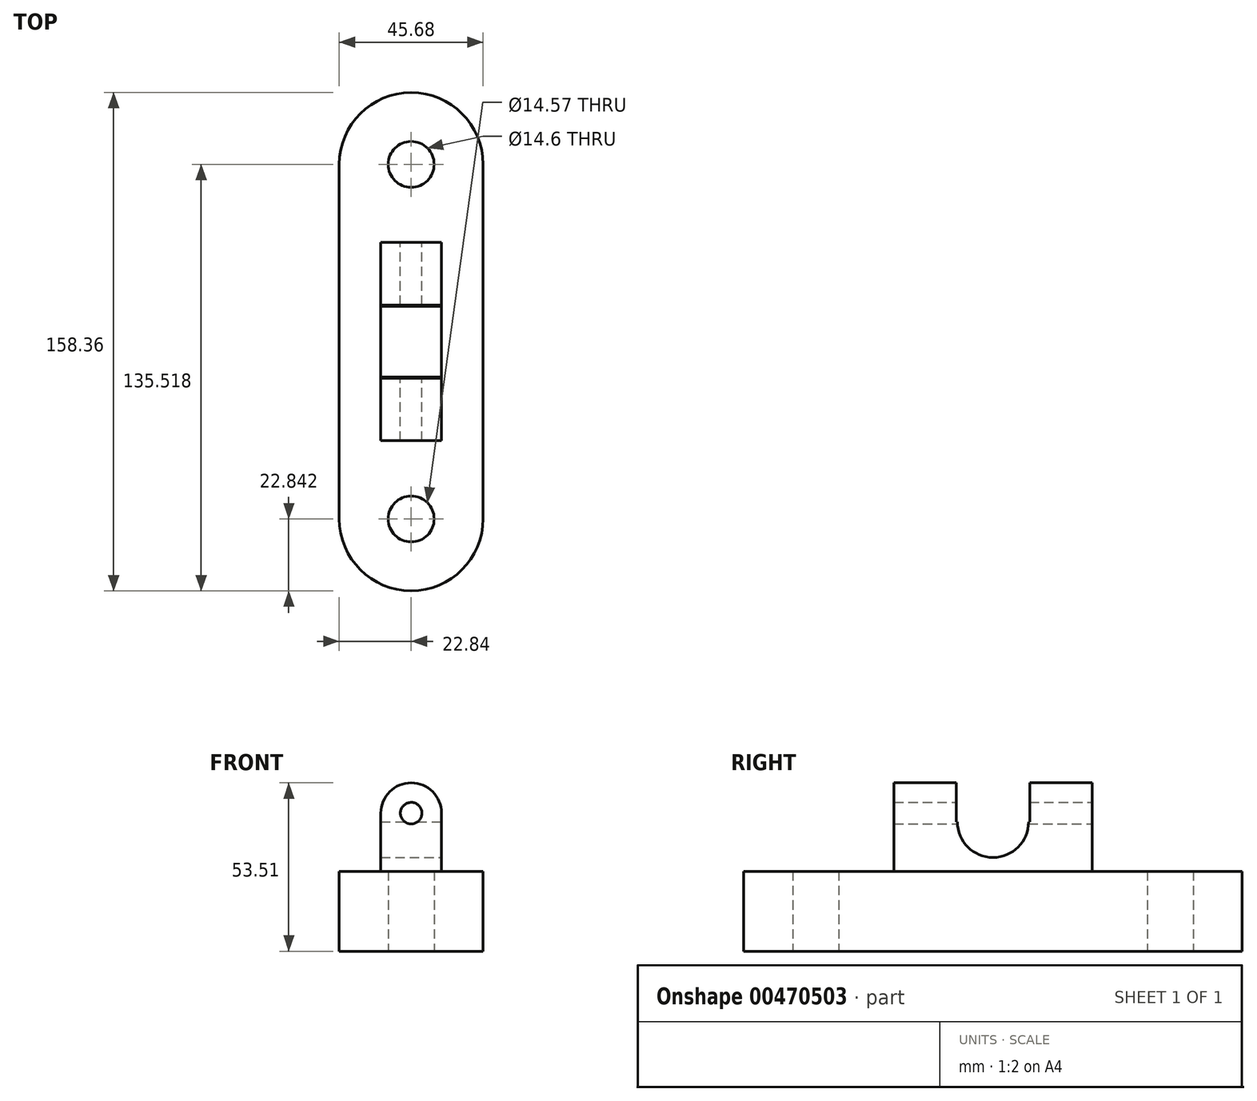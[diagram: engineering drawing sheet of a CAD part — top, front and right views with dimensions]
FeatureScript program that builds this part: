
annotation { "Feature Type Name" : "Feature", "Feature Type Description" : "" }
export const myFeature = defineFeature(function(context is Context, id is Id, definition is map)
    precondition{}
    {
        {
            var Q0;
            Q0=qCreatedBy(makeId("Top.planeOp"),FACE);
            var sketch = newSketch(context, id + "F0", { "sketchPlane" : qUnion([Q0])});
            skLineSegment(sketch, "E0.bottom", {"start": v(22.84, -56.34) * mm, "end": v(-22.84, -56.34) * mm});
            skLineSegment(sketch, "E0.top", {"start": v(22.84, 56.34) * mm, "end": v(-22.84, 56.34) * mm});
            skLineSegment(sketch, "E0.left", {"start": v(22.84, -56.34) * mm, "end": v(22.84, 56.34) * mm});
            skLineSegment(sketch, "E0.right", {"start": v(-22.84, -56.34) * mm, "end": v(-22.84, 56.34) * mm});
            skPoint(sketch, "E0.middle", {"position": v(0, 0) * mm});
            skArc(sketch, "E1", {"start": v(-22.84, 56.34) * mm, "mid": v(0, 79.18) * mm, "end": v(22.84, 56.34) * mm});
            skArc(sketch, "E2", {"start": v(-22.84, -56.34) * mm, "mid": v(0, -79.18) * mm, "end": v(22.84, -56.34) * mm});
            skCircle(sketch, "E3", {"center": v(0, -56.34) * mm, "radius": 7.29 * mm});
            skCircle(sketch, "E4", {"center": v(0, 56.34) * mm, "radius": 7.3 * mm});
            skSolve(sketch);
        }
        {
            var Q0;
            Q0 = qSketchRegion(id + "F0", true);
            extrude(context, id + "F1", {"entities" : qUnion([Q0]), "depth" : 25.4 * mm});
        }
        {
            var Q0;
            Q0=qCreatedBy(makeId("Front.planeOp"),FACE);
            var sketch = newSketch(context, id + "F2", { "sketchPlane" : qUnion([Q0])});
            skLineSegment(sketch, "E5.bottom", {"start": v(9.64, 25.4) * mm, "end": v(-9.64, 25.4) * mm});
            skLineSegment(sketch, "E5.left", {"start": v(9.64, 25.4) * mm, "end": v(9.64, 43.87) * mm});
            skLineSegment(sketch, "E5.right", {"start": v(-9.64, 25.4) * mm, "end": v(-9.64, 43.87) * mm});
            skPoint(sketch, "E5.middle", {"position": v(0, 34.63) * mm});
            skArc(sketch, "E6", {"start": v(-9.64, 43.87) * mm, "mid": v(0, 53.5) * mm, "end": v(9.64, 43.87) * mm});
            skCircle(sketch, "E7", {"center": v(0, 43.87) * mm, "radius": 3.42 * mm});
            skSolve(sketch);
        }
        {
            var Q0;
            Q0=makeQuery(id+"F2.imprint","IMPRINT",FACE,{"disambiguationData":[TD([[makeQuery(id+"F2.imprint","IMPRINT",EDGE,{"derivedFrom":sQuery(id+"F2.wireOp",EDGE,"E5.bottom")}),-1.0]])]});
            extrude(context, id + "F3", {"entities" : qUnion([Q0]), "operationType" : NewBodyOperationType.ADD, "endBound" : BoundingType.SYMMETRIC, "depth" : 63 * mm});
        }
        {
            var Q0;
            Q0=qCreatedBy(makeId("Right.planeOp"),FACE);
            var sketch = newSketch(context, id + "F4", { "sketchPlane" : qUnion([Q0])});
            skLineSegment(sketch, "E8.bottom", {"start": v(11.65, 41.06) * mm, "end": v(11.29, 41.06) * mm});
            skLineSegment(sketch, "E8.top", {"start": v(11.65, 65.96) * mm, "end": v(-11.65, 65.96) * mm});
            skLineSegment(sketch, "E8.left", {"start": v(11.65, 41.06) * mm, "end": v(11.65, 65.96) * mm});
            skLineSegment(sketch, "E8.right", {"start": v(-11.65, 41.06) * mm, "end": v(-11.65, 65.96) * mm});
            skPoint(sketch, "E8.middle", {"position": v(0, 53.5) * mm});
            skArc(sketch, "E9", {"start": v(-11.29, 41.06) * mm, "mid": v(0, 29.77) * mm, "end": v(11.29, 41.06) * mm});
            skLineSegment(sketch, "E10.trimOffspring", {"start": v(-11.29, 41.06) * mm, "end": v(-11.65, 41.06) * mm});
            skSolve(sketch);
        }
        {
            var Q0;
            Q0 = qSketchRegion(id + "F4", true);
            extrude(context, id + "F5", {"entities" : qUnion([Q0]), "operationType" : NewBodyOperationType.REMOVE, "endBound" : BoundingType.SYMMETRIC, "oppositeDirection" : true, "depth" : 72.64 * mm});
        }
    });
